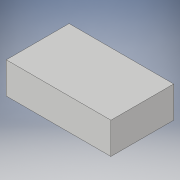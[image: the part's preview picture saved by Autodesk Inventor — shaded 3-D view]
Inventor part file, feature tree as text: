
AUTODESK INVENTOR PART (.ipt)
format: ipt  version: 2019 (Build 230136000, 136)  size: 86,016 bytes
history: native  units: in
note: dims shown in document units (in); Inventor stores cm internally (conversion verified against a paired STEP export)
features: extrude x1, sketch x1
ambient origin geometry x8: Origin, YZ Plane, XZ Plane, XY Plane, X Axis, Y Axis, Z Axis, Center Point
bodies: Solid1 (feature_tree)
feature tree (2):
  extrude  "Extrusion1"  Depth=3.0in
  sketch  "Sketch1"  dims[d0=5.0in d1=3.0in d2=1.5in d3=0.0in]
